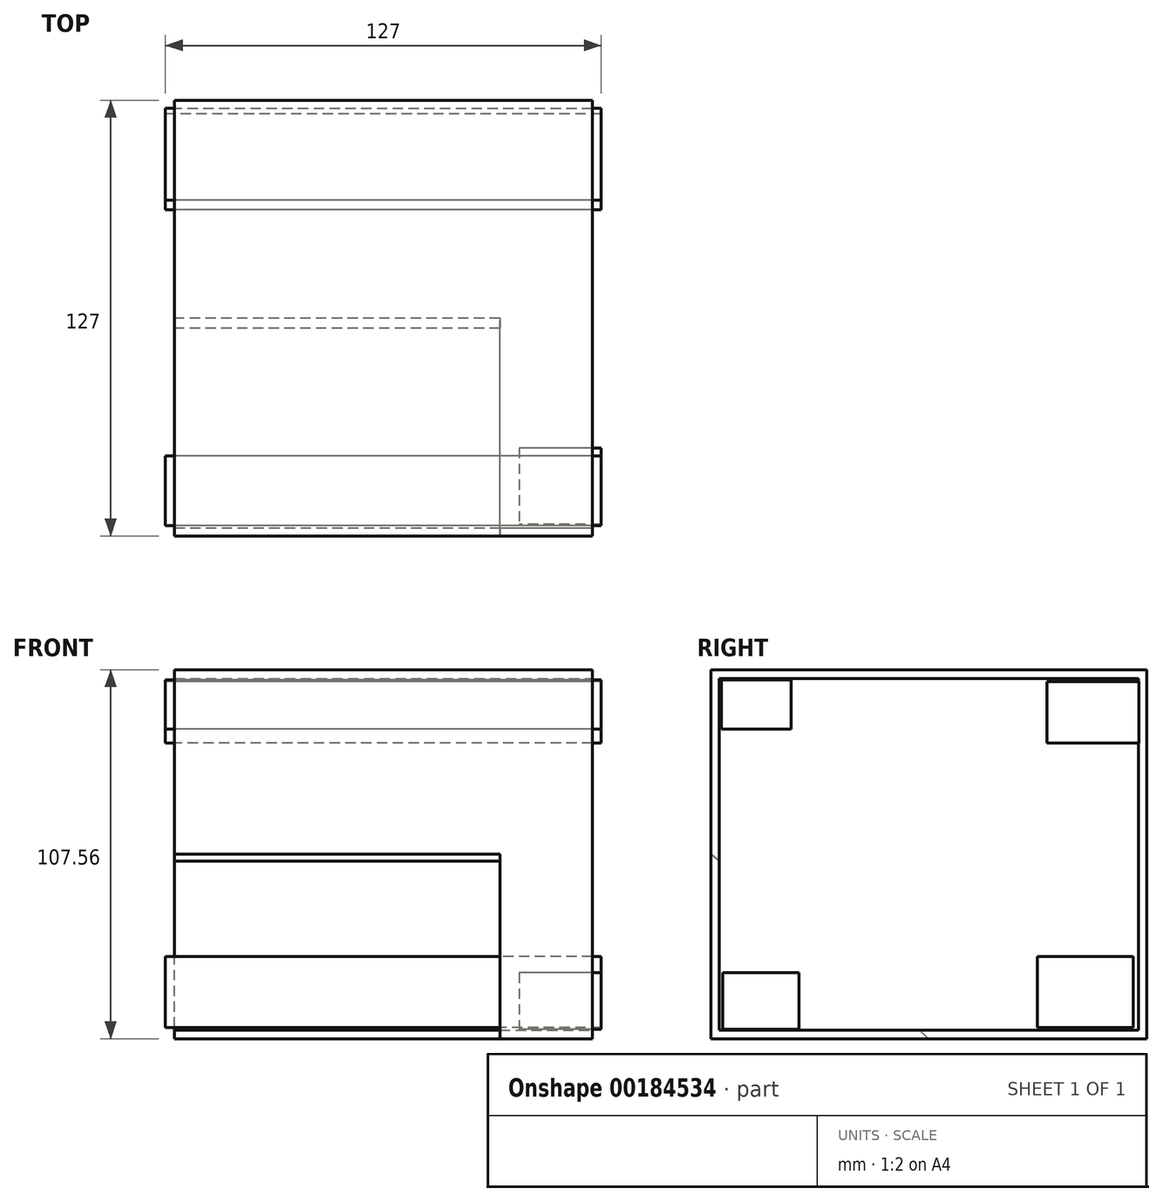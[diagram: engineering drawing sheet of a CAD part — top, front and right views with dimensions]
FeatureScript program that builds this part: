
annotation { "Feature Type Name" : "Feature", "Feature Type Description" : "" }
export const myFeature = defineFeature(function(context is Context, id is Id, definition is map)
    precondition{}
    {
        {
            var Q0;
            Q0=qCreatedBy(makeId("Front.planeOp"),FACE);
            var sketch = newSketch(context, id + "F0", { "sketchPlane" : qUnion([Q0])});
            skLineSegment(sketch, "E0.bottom", {"start": v(60.9, 53.78) * mm, "end": v(-60.9, 53.78) * mm});
            skLineSegment(sketch, "E0.top", {"start": v(60.9, -53.78) * mm, "end": v(-60.9, -53.78) * mm});
            skLineSegment(sketch, "E0.left", {"start": v(60.9, 53.78) * mm, "end": v(60.9, -53.78) * mm});
            skLineSegment(sketch, "E0.right", {"start": v(-60.9, 53.78) * mm, "end": v(-60.9, -53.78) * mm});
            skPoint(sketch, "E0.middle", {"position": v(0, 0) * mm});
            skSolve(sketch);
        }
        {
            var Q0;
            Q0=makeQuery(id+"F0.imprint","IMPRINT",FACE,{"disambiguationData":[TD([[makeQuery(id+"F0.imprint","IMPRINT",EDGE,{"derivedFrom":sQuery(id+"F0.wireOp",EDGE,"E0.bottom")}),1.0]])]});
            extrude(context, id + "F1", {"entities" : qUnion([Q0]), "endBound" : BoundingType.SYMMETRIC, "depth" : 127 * mm});
        }
        {
            var Q0;
            Q0=makeQuery(id+"F1.opExtrude","SWEPT_FACE",FACE,{"disambiguationData":[OSD([sQuery(id+"F0.wireOp",EDGE,"E0.right")])]});
            var sketch = newSketch(context, id + "F2", { "sketchPlane" : qUnion([Q0])});
            skLineSegment(sketch, "E1", {"start": v(0, -53.78) * mm, "end": v(63.5, 0) * mm});
            skLineSegment(sketch, "E2", {"start": v(63.5, 0) * mm, "end": v(63.5, -53.78) * mm});
            skLineSegment(sketch, "E3", {"start": v(63.5, -53.78) * mm, "end": v(0, -53.78) * mm});
            skSolve(sketch);
        }
        {
            var Q0;
            Q0 = qSketchRegion(id + "F2", true);
            extrude(context, id + "F3", {"entities" : qUnion([Q0]), "operationType" : NewBodyOperationType.REMOVE, "oppositeDirection" : true, "depth" : 94.87 * mm});
        }
        {
            var Q0;
            Q0=makeQuery(id+"F1.opExtrude","SWEPT_FACE",FACE,{"disambiguationData":[OSD([sQuery(id+"F0.wireOp",EDGE,"E0.left")])]});
            var sketch = newSketch(context, id + "F4", { "sketchPlane" : qUnion([Q0])});
            skLineSegment(sketch, "E4", {"start": v(-63.44, 0.01) * mm, "end": v(-0.12, -53.33) * mm});
            skLineSegment(sketch, "E5", {"start": v(-0.12, -53.33) * mm, "end": v(-63.73, -53.77) * mm});
            skLineSegment(sketch, "E6", {"start": v(-63.73, -53.77) * mm, "end": v(-63.73, 0.3) * mm});
            skSolve(sketch);
        }
        {
            var Q0;
            {var subQ0=sQuery(id+"F0.wireOp",EDGE,"E0.left");Q0=makeQuery(id+"F4.imprint","IMPRINT",FACE,{"disambiguationData":[TD([[makeQuery(id+"F4.imprint","IMPRINT",EDGE,{"derivedFrom":makeQuery(id+"F1.opExtrude","CAP_EDGE",EDGE,{"disambiguationData":[OSD([subQ0])],"isStart":true})}),-1.0]])]});}
            var sketch = newSketch(context, id + "F5", { "sketchPlane" : qUnion([Q0])});
            skLineSegment(sketch, "E7.bottom", {"start": v(61.09, -51.23) * mm, "end": v(-61.09, -51.23) * mm});
            skLineSegment(sketch, "E7.top", {"start": v(61.09, 51.23) * mm, "end": v(-61.09, 51.23) * mm});
            skLineSegment(sketch, "E7.left", {"start": v(61.09, -51.23) * mm, "end": v(61.09, 51.23) * mm});
            skLineSegment(sketch, "E7.right", {"start": v(-61.09, -51.23) * mm, "end": v(-61.09, 51.23) * mm});
            skPoint(sketch, "E7.middle", {"position": v(0, 0) * mm});
            skSolve(sketch);
        }
        {
            var Q0;
            Q0 = qSketchRegion(id + "F5", true);
            extrude(context, id + "F6", {"entities" : qUnion([Q0]), "operationType" : NewBodyOperationType.REMOVE, "oppositeDirection" : true, "depth" : 635 * mm});
        }
        {
            var Q0;
            Q0=qCreatedBy(makeId("Right.planeOp"),FACE);
            var sketch = newSketch(context, id + "F7", { "sketchPlane" : qUnion([Q0])});
            skLineSegment(sketch, "E8.bottom", {"start": v(-40.17, 50.83) * mm, "end": v(-60.53, 50.83) * mm});
            skLineSegment(sketch, "E8.top", {"start": v(-40.17, 36.48) * mm, "end": v(-60.53, 36.48) * mm});
            skLineSegment(sketch, "E8.left", {"start": v(-40.17, 50.83) * mm, "end": v(-40.17, 36.48) * mm});
            skLineSegment(sketch, "E8.right", {"start": v(-60.53, 50.83) * mm, "end": v(-60.53, 36.48) * mm});
            skPoint(sketch, "E8.middle", {"position": v(-50.35, 43.65) * mm});
            skLineSegment(sketch, "E9.bottom", {"start": v(-37.85, -34.58) * mm, "end": v(-60.07, -34.58) * mm});
            skLineSegment(sketch, "E9.top", {"start": v(-37.85, -51.01) * mm, "end": v(-60.07, -51.01) * mm});
            skLineSegment(sketch, "E9.left", {"start": v(-37.85, -34.58) * mm, "end": v(-37.85, -51.01) * mm});
            skLineSegment(sketch, "E9.right", {"start": v(-60.07, -34.58) * mm, "end": v(-60.07, -51.01) * mm});
            skPoint(sketch, "E9.middle", {"position": v(-48.96, -42.8) * mm});
            skLineSegment(sketch, "E10.bottom", {"start": v(61.15, 32.41) * mm, "end": v(34.34, 32.41) * mm});
            skLineSegment(sketch, "E10.top", {"start": v(61.15, 50.28) * mm, "end": v(34.34, 50.28) * mm});
            skLineSegment(sketch, "E10.left", {"start": v(61.15, 32.41) * mm, "end": v(61.15, 50.28) * mm});
            skLineSegment(sketch, "E10.right", {"start": v(34.34, 32.41) * mm, "end": v(34.34, 50.28) * mm});
            skPoint(sketch, "E10.middle", {"position": v(47.74, 41.35) * mm});
            skLineSegment(sketch, "E11.bottom", {"start": v(59.47, -50.53) * mm, "end": v(31.55, -50.53) * mm});
            skLineSegment(sketch, "E11.top", {"start": v(59.47, -29.86) * mm, "end": v(31.55, -29.86) * mm});
            skLineSegment(sketch, "E11.left", {"start": v(59.47, -50.53) * mm, "end": v(59.47, -29.86) * mm});
            skLineSegment(sketch, "E11.right", {"start": v(31.55, -50.53) * mm, "end": v(31.55, -29.86) * mm});
            skPoint(sketch, "E11.middle", {"position": v(45.51, -40.2) * mm});
            skSolve(sketch);
        }
        {
            var Q0;
            Q0 = qSketchRegion(id + "F7", true);
            extrude(context, id + "F8", {"entities" : qUnion([Q0]), "operationType" : NewBodyOperationType.ADD, "endBound" : BoundingType.SYMMETRIC, "depth" : 127 * mm});
        }
        {
            var Q0;
            Q0=makeQuery(id+"F8.opExtrude","CAP_FACE",FACE,{"disambiguationData":[OSD([sQuery(id+"F7.wireOp",EDGE,"E9.bottom"),sQuery(id+"F7.wireOp",EDGE,"E9.top"),sQuery(id+"F7.wireOp",EDGE,"E9.left"),sQuery(id+"F7.wireOp",EDGE,"E9.right")])],"isStart":true});
            extrude(context, id + "F9", {"entities" : qUnion([Q0]), "operationType" : NewBodyOperationType.REMOVE, "oppositeDirection" : true, "depth" : 103 * mm});
        }
    });
